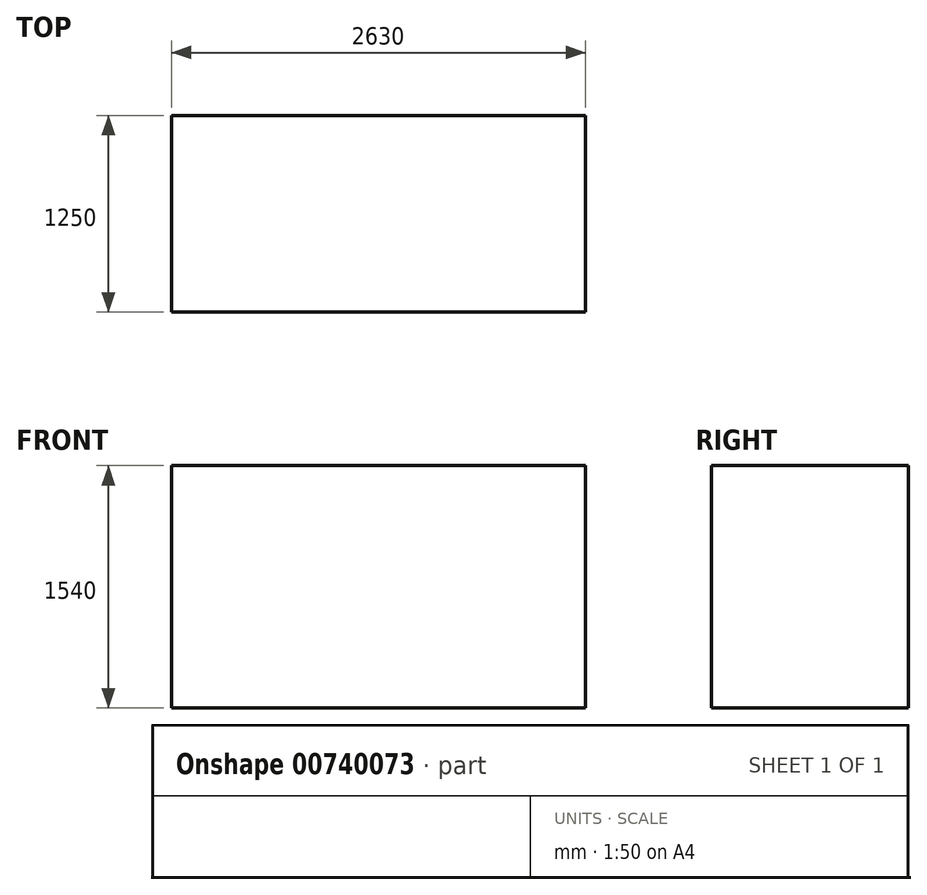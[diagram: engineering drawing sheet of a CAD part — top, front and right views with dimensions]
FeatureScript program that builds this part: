
annotation { "Feature Type Name" : "Feature", "Feature Type Description" : "" }
export const myFeature = defineFeature(function(context is Context, id is Id, definition is map)
    precondition{}
    {
        {
            var Q0;
            Q0=qCreatedBy(makeId("Front.planeOp"),FACE);
            var sketch = newSketch(context, id + "F0", { "sketchPlane" : qUnion([Q0])});
            skLineSegment(sketch, "E0.bottom", {"start": v(0, 0) * mm, "end": v(2630, 0) * mm});
            skLineSegment(sketch, "E0.top", {"start": v(0, 1540) * mm, "end": v(2630, 1540) * mm});
            skLineSegment(sketch, "E0.left", {"start": v(0, 0) * mm, "end": v(0, 1540) * mm});
            skLineSegment(sketch, "E0.right", {"start": v(2630, 0) * mm, "end": v(2630, 1540) * mm});
            skSolve(sketch);
        }
        {
            var Q0;
            Q0 = qSketchRegion(id + "F0", true);
            extrude(context, id + "F1", {"entities" : qUnion([Q0]), "depth" : 1250 * mm, "offsetDistance" : 25 * mm});
        }
    });
